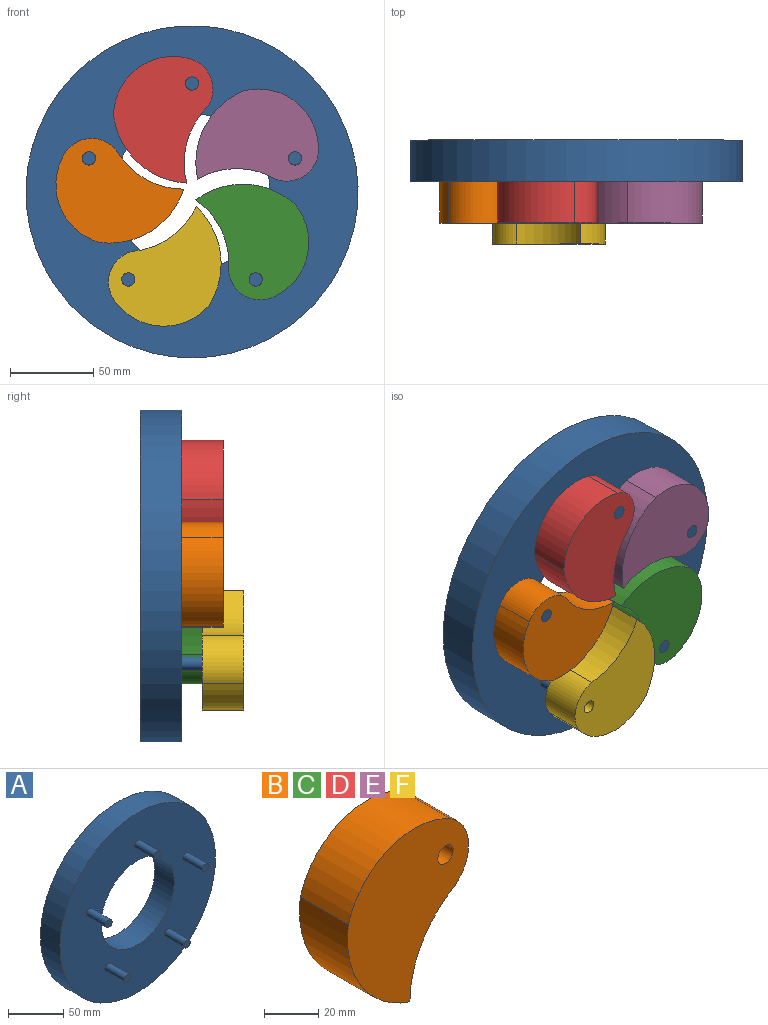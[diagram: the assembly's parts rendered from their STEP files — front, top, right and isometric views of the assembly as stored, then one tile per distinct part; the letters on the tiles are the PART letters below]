
ASSEMBLY  parts=6 mates=5
PART A: 14 faces, bbox 200x50x200 mm
  f0: cylinder r=47mm len=94mm, axis (0,1,0), area 7382.7mm2, adj f2,f3
  f1: cylinder r=100mm len=200mm, axis (0,1,0), area 15708mm2, adj f2,f3
  f2: plane 200x200mm, normal (0,-1,0), area 24224.8mm2, adj f0,f1,f4,f6,f8,f10,f12
  f3: plane 200x200mm, normal (0,1,0), area 24476.1mm2, adj f0,f1
  f4: cylinder r=4mm len=25mm, axis (0,1,0), area 628.3mm2, adj f2,f5
  f5: plane 8x8mm, normal (0,-1,0), area 50.3mm2, adj f4
  f6: cylinder r=4mm len=25mm, axis (0,1,0), area 628.3mm2, adj f2,f7
  f7: plane 8x8mm, normal (0,-1,0), area 50.3mm2, adj f6
  f8: cylinder r=4mm len=25mm, axis (0,1,0), area 628.3mm2, adj f2,f9
  f9: plane 8x8mm, normal (0,-1,0), area 50.3mm2, adj f8
  f10: cylinder r=4mm len=25mm, axis (0,1,0), area 628.3mm2, adj f2,f11
  f11: plane 8x8mm, normal (0,-1,0), area 50.3mm2, adj f10
  f12: cylinder r=4mm len=25mm, axis (0,1,0), area 628.3mm2, adj f2,f13
  f13: plane 8x8mm, normal (0,-1,0), area 50.3mm2, adj f12
PART B: 7 faces, bbox 63x25x77 mm
  f0: cylinder r=19.01mm len=31.08mm, axis (0,1,0), area 913mm2, adj f1,f3,f5,f6
  f1: cylinder r=36.06mm len=53.4mm, axis (0,1,0), area 1660.1mm2, adj f0,f2,f5,f6
  f2: cylinder r=47mm len=50.7mm, axis (0,1,0), area 1626.9mm2, adj f1,f3,f5,f6
  f3: cylinder r=47mm len=40.7mm, axis (0,1,0), area 1230.5mm2, adj f0,f2,f5,f6
  f4: cylinder r=4mm len=25mm, axis (0,1,0), area 628.3mm2, adj f5,f6
  f5: plane 77x63.02mm, normal (0,-1,0), area 3043.5mm2, adj f0,f1,f2,f3,f4
  f6: plane 77x63.02mm, normal (0,1,0), area 3043.5mm2, adj f0,f1,f2,f3,f4
PART C: same geometry as B
PART D: same geometry as B
PART E: same geometry as B
PART F: same geometry as B
PLACE A t=(-16.15,114.69,-5.89)mm
PLACE B rot(axis=(0,-1,0),90deg) t=(-21.1,89.69,-4.28)mm
PLACE C rot(axis=(0,1,0),125deg) t=(-13.94,89.69,-10.72)mm
PLACE D rot(axis=(0,-1,0),15deg) t=(-19.29,89.69,-0.6)mm
PLACE E rot(axis=(0,1,0),60deg) t=(-12.83,89.69,1.78)mm
PLACE F rot(axis=(0,-1,0),155deg) t=(-13.56,77.19,-14.76)mm
MATE revolute C.f4 <-> A.f10  axis (0,-1,0) through (22.17,64.69,-58.64)mm
MATE revolute F.f4 <-> A.f8  axis (0,1,0) through (-54.48,64.69,-58.64)mm
MATE revolute E.f4 <-> A.f12  axis (0,-1,0) through (45.86,64.69,14.26)mm
MATE revolute A.f4 <-> D.f4  axis (0,-1,0) through (-16.15,64.69,59.31)mm
MATE revolute B.f4 <-> A.f6  axis (0,1,0) through (-78.16,64.69,14.26)mm
